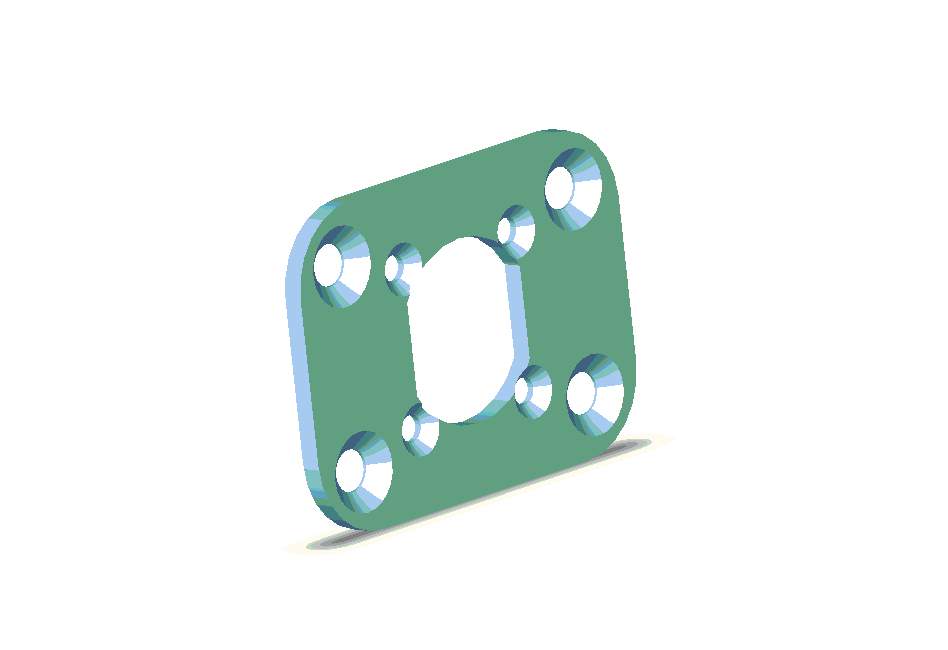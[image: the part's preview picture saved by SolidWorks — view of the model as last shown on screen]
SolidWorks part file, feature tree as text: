
SOLIDWORKS PART (.sldprt)
format: sldprt  version: not decoded by parser v0  size: 164,864 bytes
history: native  units: mm
features: chamfer x2, sketch x1, extrude x1, fillet x1 (+8 scaffold rows collapsed)
feature tree (13):
  scaffold x8  (default folders/planes/origin — collapsed)
  sketch  "Sketch1"  dims[c1.D5=14.3mm c1.D6=3.2639mm c1.D13=2.1mm c1.D14=2.1mm c1.D15=2.1mm c1.D16=2.1mm c1.D1=12.7mm c1.D2=25.4mm c1.D3=17.4625mm c1.D4=34.925mm c1.D7=4.7625mm c1.D8=4.7625mm c1.D9=4.7625mm c1.D10=4.7625mm c1.D11=0.25mm c1.D12=0.25mm c2.D13=8.75mm]
  extrude  "Base-Extrude"  Depth=1.5875mm
  fillet  "Fillet1"  Radius=6.35mm
  chamfer  "Chamfer2"  Distance=1mm Angle=45deg
  chamfer  "Chamfer3"  Distance=1.5mm Angle=42deg
decode coverage: 5 of 5 modeling features carry decoded parameters
note: suppression state not decoded; provenance and decode notes live in map.json
